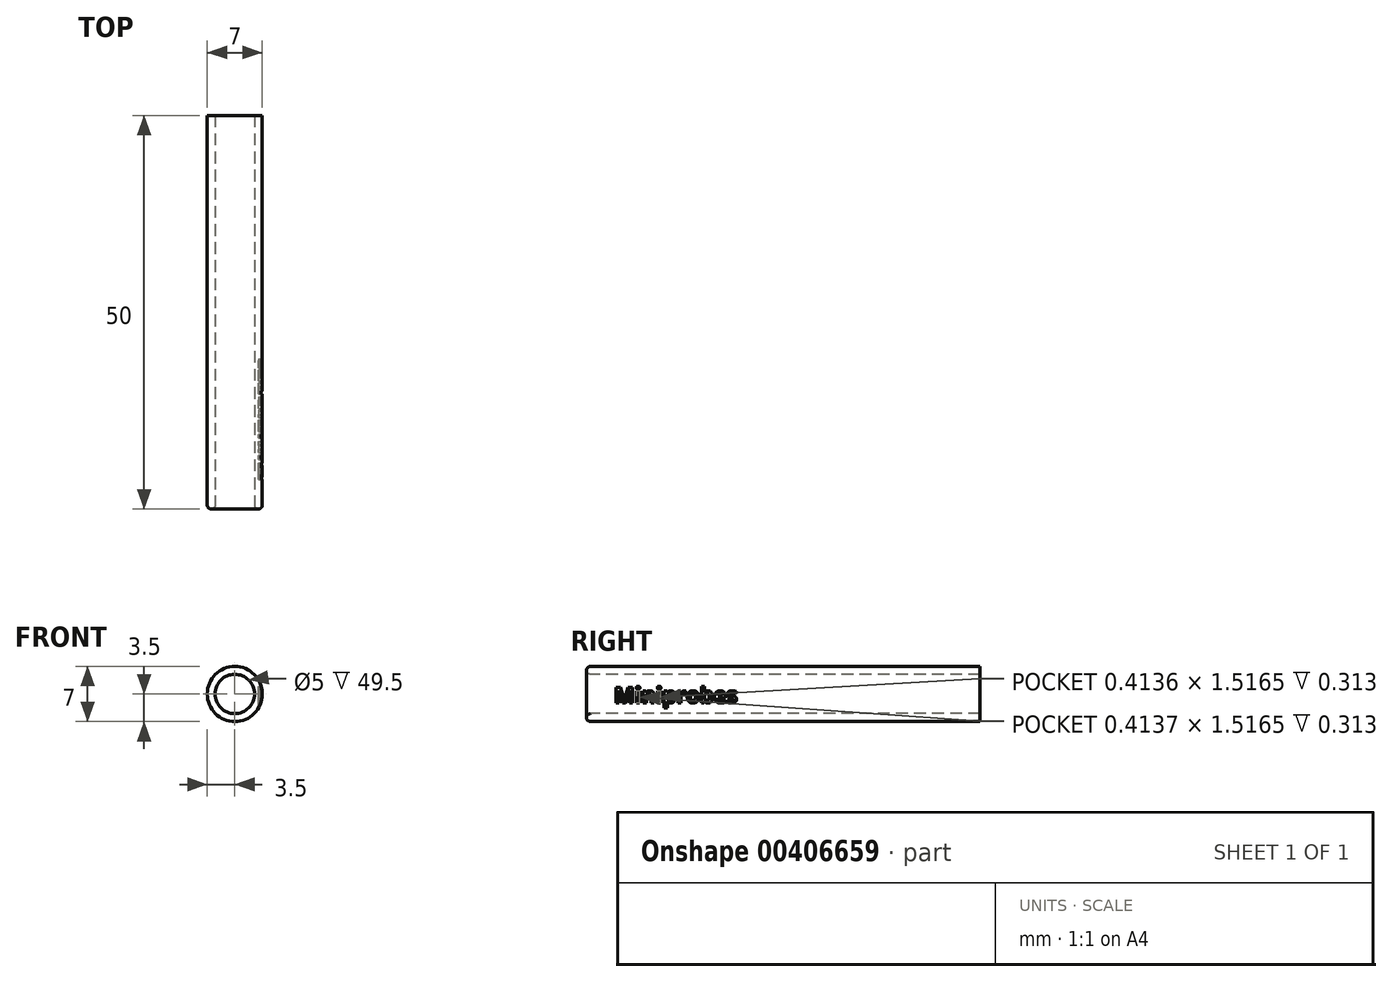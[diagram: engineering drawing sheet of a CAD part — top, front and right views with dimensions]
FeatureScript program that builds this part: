
annotation { "Feature Type Name" : "Feature", "Feature Type Description" : "" }
export const myFeature = defineFeature(function(context is Context, id is Id, definition is map)
    precondition{}
    {
        {
            var Q0;
            Q0=qCreatedBy(makeId("Front.planeOp"),FACE);
            cPlane(context, id + "F0", {"entities" : qUnion([Q0]), "cplaneType" : CPlaneType.OFFSET, "offset" : 0.5 * mm, "width" : 150 * mm, "height" : 150 * mm});
        }
        {
            var Q0;
            Q0=qCreatedBy(id+"F0.planeOp",FACE);
            var sketch = newSketch(context, id + "F1", { "sketchPlane" : qUnion([Q0])});
            skCircle(sketch, "E0", {"center": v(0, 0) * mm, "radius": 2.5 * mm});
            skCircle(sketch, "E1", {"center": v(0, 0) * mm, "radius": 3.5 * mm});
            skSolve(sketch);
        }
        {
            var Q0;
            Q0=makeQuery(id+"F1.imprint","IMPRINT",FACE,{"disambiguationData":[TD([[makeQuery(id+"F1.imprint","IMPRINT",EDGE,{"derivedFrom":sQuery(id+"F1.wireOp",EDGE,"E0")}),-1.0]])]});
            extrude(context, id + "F2", {"entities" : qUnion([Q0]), "oppositeDirection" : true, "depth" : 50 * mm, "offsetDistance" : 25 * mm});
        }
        {
            var Q0;
            Q0=makeQuery(id+"F2.opExtrude","CAP_FACE",FACE,{"disambiguationData":[OSD([sQuery(id+"F1.wireOp",EDGE,"E0"),sQuery(id+"F1.wireOp",EDGE,"E1")])],"isStart":true});
            fillet(context, id + "F3", {"entities" : qUnion([Q0]), "tangentPropagation" : true, "radius" : 0.5 * mm, "defaultsChanged" : true, "vertexSettings" : [], "allowEdgeOverflow" : false});
        }
        {
            var Q0;
            Q0=qCreatedBy(makeId("Right.planeOp"),FACE);
            cPlane(context, id + "F4", {"entities" : qUnion([Q0]), "cplaneType" : CPlaneType.OFFSET, "offset" : 4 * mm, "width" : 150 * mm, "height" : 150 * mm});
        }
        {
            var Q0;
            Q0=qCreatedBy(id+"F4.planeOp",FACE);
            var sketch = newSketch(context, id + "F5", { "sketchPlane" : qUnion([Q0])});
            skText(sketch, "E2", { "text": "Miniprobes", "fontName": "NotoSans-Bold.ttf"});
            const initialGuessF5  = {"E2": [0.003, -0.00113, 1, 0, 0.002]};
            skSetInitialGuess(sketch, initialGuessF5);
            skSolve(sketch);
        }
        {
            var Q0;
            Q0 = qSketchRegion(id + "F5", true);
            extrude(context, id + "F6", {"entities" : qUnion([Q0]), "operationType" : NewBodyOperationType.REMOVE, "oppositeDirection" : true, "depth" : 1 * mm, "offsetDistance" : 25 * mm});
        }
    });
